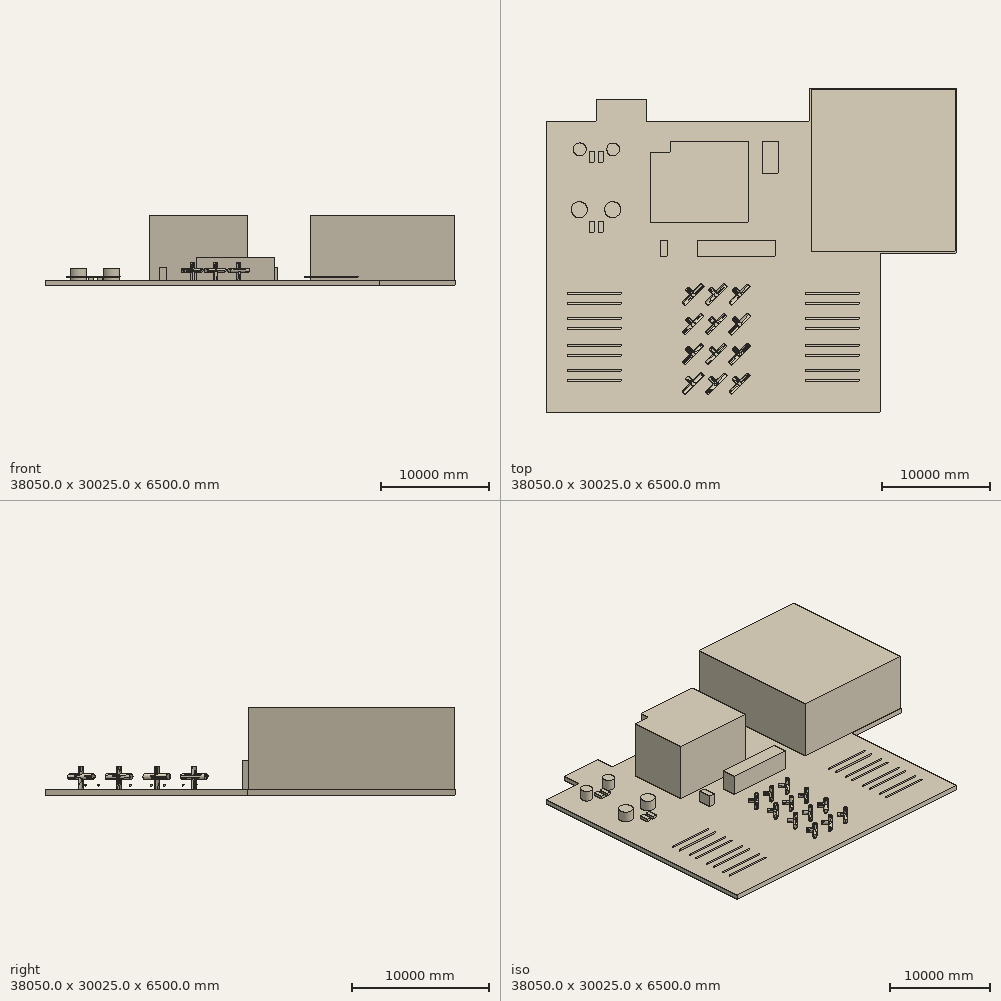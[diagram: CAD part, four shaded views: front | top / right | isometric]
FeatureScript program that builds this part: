
annotation { "Feature Type Name" : "Feature", "Feature Type Description" : "" }
export const myFeature = defineFeature(function(context is Context, id is Id, definition is map)
    precondition{}
    {
        {
            var Q0;
            Q0=qCreatedBy(makeId("Top.planeOp"),FACE);
            var sketch = newSketch(context, id + "F0", { "sketchPlane" : qUnion([Q0])});
            skLineSegment(sketch, "E0", {"start": v(0, 0) * mm, "end": v(31000, 0) * mm});
            skLineSegment(sketch, "E1", {"start": v(31000, 0) * mm, "end": v(31000, 14775) * mm});
            skLineSegment(sketch, "E2", {"start": v(31000, 14775) * mm, "end": v(38050, 14775) * mm});
            skLineSegment(sketch, "E3", {"start": v(38050, 14775) * mm, "end": v(38050, 30025) * mm});
            skLineSegment(sketch, "E4", {"start": v(38050, 30025) * mm, "end": v(24450, 30025) * mm});
            skLineSegment(sketch, "E5", {"start": v(24450, 30025) * mm, "end": v(24450, 26990) * mm});
            skLineSegment(sketch, "E6", {"start": v(24450, 26990) * mm, "end": v(0, 26990) * mm});
            skLineSegment(sketch, "E7", {"start": v(0, 26990) * mm, "end": v(0, 0) * mm});
            skLineSegment(sketch, "E8", {"start": v(4600, 26990) * mm, "end": v(4600, 28990) * mm});
            skLineSegment(sketch, "E9", {"start": v(4600, 28990) * mm, "end": v(9300, 28990) * mm});
            skLineSegment(sketch, "E10", {"start": v(9300, 28990) * mm, "end": v(9300, 26990) * mm});
            skSolve(sketch);
        }
        {
            var Q0;
            Q0=makeQuery(id+"F0.imprint","IMPRINT",FACE,{"disambiguationData":[TD([[makeQuery(id+"F0.imprint","IMPRINT",EDGE,{"derivedFrom":sQuery(id+"F0.wireOp",EDGE,"E0")}),1.0]])]});
            var Q1;
            {var subQ0=sQuery(id+"F0.wireOp",EDGE,"E8");Q1=makeQuery(id+"F0.imprint","IMPRINT",FACE,{"disambiguationData":[TD([[makeQuery(id+"F0.imprint","IMPRINT",EDGE,{"derivedFrom":subQ0}),-1.0]])]});}
            extrude(context, id + "F1", {"entities" : qUnion([Q0, Q1]), "depth" : 500 * mm, "offsetDistance" : 25 * mm});
        }
        {
            var Q0;
            Q0=makeQuery(id+"F1.opExtrude","CAP_FACE",FACE,{"disambiguationData":[OSD([sQuery(id+"F0.wireOp",EDGE,"E0"),sQuery(id+"F0.wireOp",EDGE,"E1"),sQuery(id+"F0.wireOp",EDGE,"E2"),sQuery(id+"F0.wireOp",EDGE,"E3"),sQuery(id+"F0.wireOp",EDGE,"E4"),sQuery(id+"F0.wireOp",EDGE,"E5"),sQuery(id+"F0.wireOp",EDGE,"E6"),sQuery(id+"F0.wireOp",EDGE,"E7"),sQuery(id+"F0.wireOp",EDGE,"E8"),sQuery(id+"F0.wireOp",EDGE,"E9"),sQuery(id+"F0.wireOp",EDGE,"E10")])],"isStart":false});
            var sketch = newSketch(context, id + "F2", { "sketchPlane" : qUnion([Q0])});
            skLineSegment(sketch, "E11.0", {"start": v(37950, 14875) * mm, "end": v(37950, 29925) * mm});
            skLineSegment(sketch, "E12.0", {"start": v(37950, 29925) * mm, "end": v(24550, 29925) * mm});
            skLineSegment(sketch, "E13.0", {"start": v(24550, 14875) * mm, "end": v(37950, 14875) * mm});
            skLineSegment(sketch, "E14.0", {"start": v(24550, 29925) * mm, "end": v(24550, 14875) * mm});
            skSolve(sketch);
        }
        {
            var Q0;
            Q0=makeQuery(id+"F2.imprint","IMPRINT",FACE,{"disambiguationData":[TD([[makeQuery(id+"F2.imprint","IMPRINT",EDGE,{"derivedFrom":sQuery(id+"F2.wireOp",EDGE,"E11.0")}),1.0]])]});
            extrude(context, id + "F3", {"entities" : qUnion([Q0]), "depth" : 6000 * mm, "offsetDistance" : 25 * mm});
        }
        {
            var Q0;
            Q0=makeQuery(id+"F1.opExtrude","CAP_FACE",FACE,{"disambiguationData":[OSD([sQuery(id+"F0.wireOp",EDGE,"E0"),sQuery(id+"F0.wireOp",EDGE,"E1"),sQuery(id+"F0.wireOp",EDGE,"E2"),sQuery(id+"F0.wireOp",EDGE,"E3"),sQuery(id+"F0.wireOp",EDGE,"E4"),sQuery(id+"F0.wireOp",EDGE,"E5"),sQuery(id+"F0.wireOp",EDGE,"E6"),sQuery(id+"F0.wireOp",EDGE,"E7"),sQuery(id+"F0.wireOp",EDGE,"E8"),sQuery(id+"F0.wireOp",EDGE,"E9"),sQuery(id+"F0.wireOp",EDGE,"E10")])],"isStart":false});
            var sketch = newSketch(context, id + "F4", { "sketchPlane" : qUnion([Q0])});
            skLineSegment(sketch, "E15", {"start": v(9670, 24090) * mm, "end": v(9670, 17655) * mm});
            skLineSegment(sketch, "E16", {"start": v(9670, 17655) * mm, "end": v(18770, 17655) * mm});
            skLineSegment(sketch, "E17", {"start": v(18770, 17655) * mm, "end": v(18770, 25140) * mm});
            skLineSegment(sketch, "E18", {"start": v(18770, 25140) * mm, "end": v(11520, 25140) * mm});
            skLineSegment(sketch, "E19", {"start": v(11520, 25140) * mm, "end": v(11520, 24090) * mm});
            skLineSegment(sketch, "E20", {"start": v(11520, 24090) * mm, "end": v(9670, 24090) * mm});
            skSolve(sketch);
        }
        {
            var Q0;
            Q0=makeQuery(id+"F4.imprint","IMPRINT",FACE,{"disambiguationData":[TD([[makeQuery(id+"F4.imprint","IMPRINT",EDGE,{"derivedFrom":sQuery(id+"F4.wireOp",EDGE,"E15")}),1.0]])]});
            extrude(context, id + "F5", {"entities" : qUnion([Q0]), "depth" : 6000 * mm, "offsetDistance" : 25 * mm});
        }
        {
            var Q0;
            Q0=makeQuery(id+"F1.opExtrude","CAP_FACE",FACE,{"disambiguationData":[OSD([sQuery(id+"F0.wireOp",EDGE,"E0"),sQuery(id+"F0.wireOp",EDGE,"E1"),sQuery(id+"F0.wireOp",EDGE,"E2"),sQuery(id+"F0.wireOp",EDGE,"E3"),sQuery(id+"F0.wireOp",EDGE,"E4"),sQuery(id+"F0.wireOp",EDGE,"E5"),sQuery(id+"F0.wireOp",EDGE,"E6"),sQuery(id+"F0.wireOp",EDGE,"E7"),sQuery(id+"F0.wireOp",EDGE,"E8"),sQuery(id+"F0.wireOp",EDGE,"E9"),sQuery(id+"F0.wireOp",EDGE,"E10")])],"isStart":false});
            var sketch = newSketch(context, id + "F6", { "sketchPlane" : qUnion([Q0])});
            skLineSegment(sketch, "E21.bottom", {"start": v(14054, 15955) * mm, "end": v(21254, 15955) * mm});
            skLineSegment(sketch, "E21.top", {"start": v(14054, 14455) * mm, "end": v(21254, 14455) * mm});
            skLineSegment(sketch, "E21.left", {"start": v(14054, 15955) * mm, "end": v(14054, 14455) * mm});
            skLineSegment(sketch, "E21.right", {"start": v(21254, 15955) * mm, "end": v(21254, 14455) * mm});
            skSolve(sketch);
        }
        {
            var Q0;
            Q0=makeQuery(id+"F6.imprint","IMPRINT",FACE,{"disambiguationData":[TD([[makeQuery(id+"F6.imprint","IMPRINT",EDGE,{"derivedFrom":sQuery(id+"F6.wireOp",EDGE,"E21.bottom")}),-1.0]])]});
            extrude(context, id + "F7", {"entities" : qUnion([Q0]), "depth" : 2100 * mm, "offsetDistance" : 25 * mm});
        }
        {
            var Q0;
            Q0=makeQuery(id+"F1.opExtrude","CAP_FACE",FACE,{"disambiguationData":[OSD([sQuery(id+"F0.wireOp",EDGE,"E0"),sQuery(id+"F0.wireOp",EDGE,"E1"),sQuery(id+"F0.wireOp",EDGE,"E2"),sQuery(id+"F0.wireOp",EDGE,"E3"),sQuery(id+"F0.wireOp",EDGE,"E4"),sQuery(id+"F0.wireOp",EDGE,"E5"),sQuery(id+"F0.wireOp",EDGE,"E6"),sQuery(id+"F0.wireOp",EDGE,"E7"),sQuery(id+"F0.wireOp",EDGE,"E8"),sQuery(id+"F0.wireOp",EDGE,"E9"),sQuery(id+"F0.wireOp",EDGE,"E10")])],"isStart":false});
            var sketch = newSketch(context, id + "F8", { "sketchPlane" : qUnion([Q0])});
            skLineSegment(sketch, "E22.bottom", {"start": v(2000, 25190) * mm, "end": v(7300, 25190) * mm});
            skLineSegment(sketch, "E22.top", {"start": v(2000, 22390) * mm, "end": v(7300, 22390) * mm});
            skLineSegment(sketch, "E22.left", {"start": v(2000, 25190) * mm, "end": v(2000, 22390) * mm});
            skLineSegment(sketch, "E22.right", {"start": v(7300, 25190) * mm, "end": v(7300, 22390) * mm});
            skLineSegment(sketch, "E23.bottom", {"start": v(1955.55, 19990) * mm, "end": v(7255.55, 19990) * mm});
            skLineSegment(sketch, "E23.top", {"start": v(1955.55, 16190) * mm, "end": v(7255.55, 16190) * mm});
            skLineSegment(sketch, "E23.left", {"start": v(1955.55, 19990) * mm, "end": v(1955.55, 16190) * mm});
            skLineSegment(sketch, "E23.right", {"start": v(7255.55, 19990) * mm, "end": v(7255.55, 16190) * mm});
            skCircle(sketch, "E24", {"center": v(3100, 24390) * mm, "radius": 600 * mm});
            skCircle(sketch, "E25", {"center": v(6200, 24390) * mm, "radius": 600 * mm});
            skCircle(sketch, "E26", {"center": v(3055.55, 18790) * mm, "radius": 750 * mm});
            skCircle(sketch, "E27", {"center": v(6155.55, 18790) * mm, "radius": 750 * mm});
            skSolve(sketch);
        }
        {
            var Q0;
            Q0=makeQuery(id+"F8.imprint","IMPRINT",FACE,{"disambiguationData":[TD([[makeQuery(id+"F8.imprint","IMPRINT",EDGE,{"derivedFrom":sQuery(id+"F8.wireOp",EDGE,"E24")}),1.0]])]});
            var Q1;
            Q1=makeQuery(id+"F8.imprint","IMPRINT",FACE,{"disambiguationData":[TD([[makeQuery(id+"F8.imprint","IMPRINT",EDGE,{"derivedFrom":sQuery(id+"F8.wireOp",EDGE,"E25")}),1.0]])]});
            var Q2;
            Q2=makeQuery(id+"F8.imprint","IMPRINT",FACE,{"disambiguationData":[TD([[makeQuery(id+"F8.imprint","IMPRINT",EDGE,{"derivedFrom":sQuery(id+"F8.wireOp",EDGE,"E26")}),1.0]])]});
            var Q3;
            Q3=makeQuery(id+"F8.imprint","IMPRINT",FACE,{"disambiguationData":[TD([[makeQuery(id+"F8.imprint","IMPRINT",EDGE,{"derivedFrom":sQuery(id+"F8.wireOp",EDGE,"E27")}),1.0]])]});
            extrude(context, id + "F9", {"entities" : qUnion([Q0, Q1, Q2, Q3]), "depth" : 1100 * mm, "offsetDistance" : 25 * mm});
        }
        {
            var Q0;
            Q0=makeQuery(id+"F1.opExtrude","CAP_FACE",FACE,{"disambiguationData":[OSD([sQuery(id+"F0.wireOp",EDGE,"E0"),sQuery(id+"F0.wireOp",EDGE,"E1"),sQuery(id+"F0.wireOp",EDGE,"E2"),sQuery(id+"F0.wireOp",EDGE,"E3"),sQuery(id+"F0.wireOp",EDGE,"E4"),sQuery(id+"F0.wireOp",EDGE,"E5"),sQuery(id+"F0.wireOp",EDGE,"E6"),sQuery(id+"F0.wireOp",EDGE,"E7"),sQuery(id+"F0.wireOp",EDGE,"E8"),sQuery(id+"F0.wireOp",EDGE,"E9"),sQuery(id+"F0.wireOp",EDGE,"E10")])],"isStart":false});
            var sketch = newSketch(context, id + "F10", { "sketchPlane" : qUnion([Q0])});
            skLineSegment(sketch, "E28.bottom", {"start": v(4000, 24190) * mm, "end": v(4500, 24190) * mm});
            skLineSegment(sketch, "E28.top", {"start": v(4000, 23190) * mm, "end": v(4500, 23190) * mm});
            skLineSegment(sketch, "E28.left", {"start": v(4000, 24190) * mm, "end": v(4000, 23190) * mm});
            skLineSegment(sketch, "E28.right", {"start": v(4500, 24190) * mm, "end": v(4500, 23190) * mm});
            skLineSegment(sketch, "E29.bottom", {"start": v(4800, 24190) * mm, "end": v(5300, 24190) * mm});
            skLineSegment(sketch, "E29.top", {"start": v(4800, 23190) * mm, "end": v(5300, 23190) * mm});
            skLineSegment(sketch, "E29.left", {"start": v(4800, 24190) * mm, "end": v(4800, 23190) * mm});
            skLineSegment(sketch, "E29.right", {"start": v(5300, 24190) * mm, "end": v(5300, 23190) * mm});
            skLineSegment(sketch, "E30.bottom", {"start": v(3980.54, 17694.12) * mm, "end": v(4480.54, 17694.12) * mm});
            skLineSegment(sketch, "E30.top", {"start": v(3980.54, 16694.12) * mm, "end": v(4480.54, 16694.12) * mm});
            skLineSegment(sketch, "E30.left", {"start": v(3980.54, 17694.12) * mm, "end": v(3980.54, 16694.12) * mm});
            skLineSegment(sketch, "E30.right", {"start": v(4480.54, 17694.12) * mm, "end": v(4480.54, 16694.12) * mm});
            skLineSegment(sketch, "E31.bottom", {"start": v(4780.54, 17694.12) * mm, "end": v(5280.54, 17694.12) * mm});
            skLineSegment(sketch, "E31.top", {"start": v(4780.54, 16694.12) * mm, "end": v(5280.54, 16694.12) * mm});
            skLineSegment(sketch, "E31.left", {"start": v(4780.54, 17694.12) * mm, "end": v(4780.54, 16694.12) * mm});
            skLineSegment(sketch, "E31.right", {"start": v(5280.54, 17694.12) * mm, "end": v(5280.54, 16694.12) * mm});
            skSolve(sketch);
        }
        {
            var Q0;
            Q0=makeQuery(id+"F10.imprint","IMPRINT",FACE,{"disambiguationData":[TD([[makeQuery(id+"F10.imprint","IMPRINT",EDGE,{"derivedFrom":sQuery(id+"F10.wireOp",EDGE,"E28.bottom")}),-1.0]])]});
            var Q1;
            Q1=makeQuery(id+"F10.imprint","IMPRINT",FACE,{"disambiguationData":[TD([[makeQuery(id+"F10.imprint","IMPRINT",EDGE,{"derivedFrom":sQuery(id+"F10.wireOp",EDGE,"E29.bottom")}),-1.0]])]});
            var Q2;
            Q2=makeQuery(id+"F10.imprint","IMPRINT",FACE,{"disambiguationData":[TD([[makeQuery(id+"F10.imprint","IMPRINT",EDGE,{"derivedFrom":sQuery(id+"F10.wireOp",EDGE,"E30.bottom")}),-1.0]])]});
            var Q3;
            Q3=makeQuery(id+"F10.imprint","IMPRINT",FACE,{"disambiguationData":[TD([[makeQuery(id+"F10.imprint","IMPRINT",EDGE,{"derivedFrom":sQuery(id+"F10.wireOp",EDGE,"E31.bottom")}),-1.0]])]});
            extrude(context, id + "F11", {"entities" : qUnion([Q0, Q1, Q2, Q3]), "depth" : 300 * mm, "offsetDistance" : 25 * mm});
        }
        {
            var Q0;
            Q0=makeQuery(id+"F1.opExtrude","CAP_FACE",FACE,{"disambiguationData":[OSD([sQuery(id+"F0.wireOp",EDGE,"E0"),sQuery(id+"F0.wireOp",EDGE,"E1"),sQuery(id+"F0.wireOp",EDGE,"E2"),sQuery(id+"F0.wireOp",EDGE,"E3"),sQuery(id+"F0.wireOp",EDGE,"E4"),sQuery(id+"F0.wireOp",EDGE,"E5"),sQuery(id+"F0.wireOp",EDGE,"E6"),sQuery(id+"F0.wireOp",EDGE,"E7"),sQuery(id+"F0.wireOp",EDGE,"E8"),sQuery(id+"F0.wireOp",EDGE,"E9"),sQuery(id+"F0.wireOp",EDGE,"E10")])],"isStart":false});
            var sketch = newSketch(context, id + "F12", { "sketchPlane" : qUnion([Q0])});
            skLineSegment(sketch, "E32", {"start": v(0, 0) * mm, "end": v(13620, 0) * mm, "construction": true});
            skLineSegment(sketch, "E33", {"start": v(13620, 0) * mm, "end": v(13620, 2628) * mm, "construction": true});
            skCircle(sketch, "E34", {"center": v(13620, 2628) * mm, "radius": 190.5 * mm});
            skSolve(sketch);
        }
        {
            var Q0;
            Q0=makeQuery(id+"F12.imprint","IMPRINT",FACE,{"disambiguationData":[TD([[makeQuery(id+"F12.imprint","IMPRINT",EDGE,{"derivedFrom":sQuery(id+"F12.wireOp",EDGE,"E34")}),1.0]])]});
            extrude(context, id + "F13", {"entities" : qUnion([Q0]), "depth" : 1615 * mm, "offsetDistance" : 25 * mm});
        }
        {
            var Q0;
            Q0=makeQuery(id+"F1.opExtrude","CAP_FACE",FACE,{"disambiguationData":[OSD([sQuery(id+"F0.wireOp",EDGE,"E0"),sQuery(id+"F0.wireOp",EDGE,"E1"),sQuery(id+"F0.wireOp",EDGE,"E2"),sQuery(id+"F0.wireOp",EDGE,"E3"),sQuery(id+"F0.wireOp",EDGE,"E4"),sQuery(id+"F0.wireOp",EDGE,"E5"),sQuery(id+"F0.wireOp",EDGE,"E6"),sQuery(id+"F0.wireOp",EDGE,"E7"),sQuery(id+"F0.wireOp",EDGE,"E8"),sQuery(id+"F0.wireOp",EDGE,"E9"),sQuery(id+"F0.wireOp",EDGE,"E10")])],"isStart":false});
            var sketch = newSketch(context, id + "F14", { "sketchPlane" : qUnion([Q0])});
            skCircle(sketch, "E35", {"center": v(15123.7, 3486.6) * mm, "radius": 209.5 * mm});
            skSolve(sketch);
        }
        {
            var Q0;
            Q0=makeQuery(id+"F14.imprint","IMPRINT",FACE,{"disambiguationData":[TD([[makeQuery(id+"F14.imprint","IMPRINT",EDGE,{"derivedFrom":sQuery(id+"F14.wireOp",EDGE,"E35")}),1.0]])]});
            extrude(context, id + "F15", {"entities" : qUnion([Q0]), "depth" : 2458 * mm, "offsetDistance" : 25 * mm});
        }
        {
            var Q0;
            Q0=makeQuery(id+"F15.opExtrude","SWEPT_BODY",BODY,{"disambiguationData":[OSD([sQuery(id+"F14.wireOp",EDGE,"E35")])]});
            var Q1;
            Q1=makeQuery(id+"F1.opExtrude","CAP_EDGE",EDGE,{"disambiguationData":[OSD([sQuery(id+"F0.wireOp",EDGE,"E0")])],"isStart":false});
            transform(context, id + "F16", {"entities" : qUnion([Q0]), "transformType" : TransformType.ROTATION, "transformAxis" : qUnion([Q1]), "angle" : 90 * degree, "makeCopy" : false});
        }
        {
            var Q0;
            Q0=makeQuery(id+"F15.opExtrude","SWEPT_BODY",BODY,{"disambiguationData":[OSD([sQuery(id+"F14.wireOp",EDGE,"E35")])]});
            transform(context, id + "F17", {"entities" : qUnion([Q0]), "transformType" : TransformType.TRANSLATION_3D, "dx" : -1510 * mm, "dy" : 3860 * mm, "dz" : -2600 * mm, "makeCopy" : false});
        }
        {
            var Q0;
            Q0=makeQuery(id+"F15.opExtrude","SWEPT_BODY",BODY,{"disambiguationData":[OSD([sQuery(id+"F14.wireOp",EDGE,"E35")])]});
            transform(context, id + "F18", {"entities" : qUnion([Q0]), "transformType" : TransformType.TRANSLATION_3D, "dx" : 0 * mm, "dy" : 0 * mm, "dz" : 939 * mm, "makeCopy" : false});
        }
        {
            var Q0;
            Q0=makeQuery(id+"F15.opExtrude","SWEPT_BODY",BODY,{"disambiguationData":[OSD([sQuery(id+"F14.wireOp",EDGE,"E35")])]});
            transform(context, id + "F19", {"entities" : qUnion([Q0]), "transformType" : TransformType.TRANSLATION_3D, "dx" : 0 * mm, "dy" : 0 * mm, "dz" : -930 * mm, "makeCopy" : false});
        }
        {
            var Q0;
            Q0=makeQuery(id+"F15.opExtrude","SWEPT_BODY",BODY,{"disambiguationData":[OSD([sQuery(id+"F14.wireOp",EDGE,"E35")])]});
            var Q1;
            Q1=makeQuery(id+"F13.opExtrude","SWEPT_FACE",FACE,{"disambiguationData":[OSD([sQuery(id+"F12.wireOp",EDGE,"E34")])]});
            transform(context, id + "F20", {"entities" : qUnion([Q0]), "transformType" : TransformType.ROTATION, "transformAxis" : qUnion([Q1]), "angle" : 45 * degree, "makeCopy" : false});
        }
        {
            var Q0;
            Q0=makeQuery(id+"F1.opExtrude","CAP_FACE",FACE,{"disambiguationData":[OSD([sQuery(id+"F0.wireOp",EDGE,"E0"),sQuery(id+"F0.wireOp",EDGE,"E1"),sQuery(id+"F0.wireOp",EDGE,"E2"),sQuery(id+"F0.wireOp",EDGE,"E3"),sQuery(id+"F0.wireOp",EDGE,"E4"),sQuery(id+"F0.wireOp",EDGE,"E5"),sQuery(id+"F0.wireOp",EDGE,"E6"),sQuery(id+"F0.wireOp",EDGE,"E7"),sQuery(id+"F0.wireOp",EDGE,"E8"),sQuery(id+"F0.wireOp",EDGE,"E9"),sQuery(id+"F0.wireOp",EDGE,"E10")])],"isStart":false});
            var sketch = newSketch(context, id + "F21", { "sketchPlane" : qUnion([Q0])});
            skCircle(sketch, "E36", {"center": v(10922.38, 1929.03) * mm, "radius": 207 * mm});
            skSolve(sketch);
        }
        {
            var Q0;
            Q0=makeQuery(id+"F21.imprint","IMPRINT",FACE,{"disambiguationData":[TD([[makeQuery(id+"F21.imprint","IMPRINT",EDGE,{"derivedFrom":sQuery(id+"F21.wireOp",EDGE,"E36")}),1.0]])]});
            extrude(context, id + "F22", {"entities" : qUnion([Q0]), "depth" : 955 * mm, "offsetDistance" : 25 * mm});
        }
        {
            var Q0;
            Q0=makeQuery(id+"F22.opExtrude","SWEPT_BODY",BODY,{"disambiguationData":[OSD([sQuery(id+"F21.wireOp",EDGE,"E36")])]});
            var Q1;
            Q1=makeQuery(id+"F1.opExtrude","CAP_EDGE",EDGE,{"disambiguationData":[OSD([sQuery(id+"F0.wireOp",EDGE,"E0")])],"isStart":false});
            transform(context, id + "F23", {"entities" : qUnion([Q0]), "transformType" : TransformType.ROTATION, "transformAxis" : qUnion([Q1]), "angle" : 90 * degree, "makeCopy" : false});
        }
        {
            var Q0;
            Q0=makeQuery(id+"F22.opExtrude","SWEPT_BODY",BODY,{"disambiguationData":[OSD([sQuery(id+"F21.wireOp",EDGE,"E36")])]});
            transform(context, id + "F24", {"entities" : qUnion([Q0]), "transformType" : TransformType.TRANSLATION_3D, "dx" : 2700 * mm, "dy" : 3450 * mm, "dz" : -1023 * mm, "makeCopy" : false});
        }
        {
            var Q0;
            Q0=makeQuery(id+"F22.opExtrude","SWEPT_BODY",BODY,{"disambiguationData":[OSD([sQuery(id+"F21.wireOp",EDGE,"E36")])]});
            var Q1;
            Q1=makeQuery(id+"F13.opExtrude","SWEPT_FACE",FACE,{"disambiguationData":[OSD([sQuery(id+"F12.wireOp",EDGE,"E34")])]});
            transform(context, id + "F25", {"entities" : qUnion([Q0]), "transformType" : TransformType.ROTATION, "transformAxis" : qUnion([Q1]), "angle" : 315 * degree, "makeCopy" : false});
        }
        {
            var Q0;
            Q0=makeQuery(id+"F15.opExtrude","SWEPT_BODY",BODY,{"disambiguationData":[OSD([sQuery(id+"F14.wireOp",EDGE,"E35")])]});
            var Q1;
            Q1=makeQuery(id+"F22.opExtrude","SWEPT_BODY",BODY,{"disambiguationData":[OSD([sQuery(id+"F21.wireOp",EDGE,"E36")])]});
            var Q2;
            Q2=makeQuery(id+"F13.opExtrude","SWEPT_BODY",BODY,{"disambiguationData":[OSD([sQuery(id+"F12.wireOp",EDGE,"E34")])]});
            booleanBodies(context, id + "F26", {"operationType" : BooleanOperationType.UNION, "tools" : qUnion([Q0, Q1, Q2])});
        }
        {
            var Q0;
            Q0=makeQuery(id+"F1.opExtrude","CAP_FACE",FACE,{"disambiguationData":[OSD([sQuery(id+"F0.wireOp",EDGE,"E0"),sQuery(id+"F0.wireOp",EDGE,"E1"),sQuery(id+"F0.wireOp",EDGE,"E2"),sQuery(id+"F0.wireOp",EDGE,"E3"),sQuery(id+"F0.wireOp",EDGE,"E4"),sQuery(id+"F0.wireOp",EDGE,"E5"),sQuery(id+"F0.wireOp",EDGE,"E6"),sQuery(id+"F0.wireOp",EDGE,"E7"),sQuery(id+"F0.wireOp",EDGE,"E8"),sQuery(id+"F0.wireOp",EDGE,"E9"),sQuery(id+"F0.wireOp",EDGE,"E10")])],"isStart":false});
            var sketch = newSketch(context, id + "F27", { "sketchPlane" : qUnion([Q0])});
            skLineSegment(sketch, "E37", {"start": v(0, 0) * mm, "end": v(15500, 0) * mm, "construction": true});
            skLineSegment(sketch, "E38", {"start": v(15500, 0) * mm, "end": v(15500, 2628) * mm, "construction": true});
            skLineSegment(sketch, "E39", {"start": v(15500, 2628) * mm, "end": v(17938, 2628) * mm, "construction": true});
            skSolve(sketch);
        }
        {
            var Q0;
            Q0=makeQuery(id+"F15.opExtrude","SWEPT_BODY",BODY,{"disambiguationData":[OSD([sQuery(id+"F14.wireOp",EDGE,"E35")])]});
            transform(context, id + "F28", {"entities" : qUnion([Q0]), "transformType" : TransformType.COPY});
        }
        {
            var Q0;
            Q0=makeQuery(id+"F15.opExtrude","SWEPT_BODY",BODY,{"disambiguationData":[OSD([sQuery(id+"F14.wireOp",EDGE,"E35")])]});
            var Q1;
            Q1=makeQuery(id+"F28.opPattern","COPY",BODY,{"derivedFrom":makeQuery(id+"F15.opExtrude","SWEPT_BODY",BODY,{"disambiguationData":[OSD([sQuery(id+"F14.wireOp",EDGE,"E35")])]}),"instanceName":"1"});
            transform(context, id + "F29", {"entities" : qUnion([Q0, Q1]), "transformType" : TransformType.TRANSLATION_3D, "dx" : 1882 * mm, "dy" : 0 * mm, "dz" : 0 * mm, "makeCopy" : true});
        }
        {
            var Q0;
            Q0=makeQuery(id+"F29.opPattern","COPY",BODY,{"derivedFrom":makeQuery(id+"F15.opExtrude","SWEPT_BODY",BODY,{"disambiguationData":[OSD([sQuery(id+"F14.wireOp",EDGE,"E35")])]}),"instanceName":"1"});
            var Q1;
            Q1=makeQuery(id+"F29.opPattern","COPY",BODY,{"derivedFrom":makeQuery(id+"F28.opPattern","COPY",BODY,{"derivedFrom":makeQuery(id+"F15.opExtrude","SWEPT_BODY",BODY,{"disambiguationData":[OSD([sQuery(id+"F14.wireOp",EDGE,"E35")])]}),"instanceName":"1"}),"instanceName":"1"});
            transform(context, id + "F30", {"entities" : qUnion([Q0, Q1]), "transformType" : TransformType.TRANSLATION_3D, "dx" : 2436 * mm, "dy" : 0 * mm, "dz" : 0 * mm, "makeCopy" : true});
        }
        {
            var Q0;
            Q0=makeQuery(id+"F29.opPattern","COPY",BODY,{"derivedFrom":makeQuery(id+"F15.opExtrude","SWEPT_BODY",BODY,{"disambiguationData":[OSD([sQuery(id+"F14.wireOp",EDGE,"E35")])]}),"instanceName":"1"});
            var Q1;
            Q1=makeQuery(id+"F29.opPattern","COPY",BODY,{"derivedFrom":makeQuery(id+"F28.opPattern","COPY",BODY,{"derivedFrom":makeQuery(id+"F15.opExtrude","SWEPT_BODY",BODY,{"disambiguationData":[OSD([sQuery(id+"F14.wireOp",EDGE,"E35")])]}),"instanceName":"1"}),"instanceName":"1"});
            transform(context, id + "F31", {"entities" : qUnion([Q0, Q1]), "transformType" : TransformType.TRANSLATION_3D, "dx" : 260 * mm, "dy" : 0 * mm, "dz" : 0 * mm, "makeCopy" : false});
        }
        {
            var Q0;
            Q0=makeQuery(id+"F27.imprint","IMPRINT",FACE,{"disambiguationData":[TD([[makeQuery(id+"F27.imprint","IMPRINT",EDGE,{"derivedFrom":makeQuery(id+"F1.opExtrude","CAP_EDGE",EDGE,{"disambiguationData":[OSD([sQuery(id+"F0.wireOp",EDGE,"E0")])],"isStart":false})}),1.0]])]});
            var sketch = newSketch(context, id + "F32", { "sketchPlane" : qUnion([Q0])});
            skLineSegment(sketch, "E40", {"start": v(15494.88, 2638.74) * mm, "end": v(15494.88, 5381.74) * mm, "construction": true});
            skLineSegment(sketch, "E41", {"start": v(15494.88, 5381.74) * mm, "end": v(15494.88, 8124.74) * mm, "construction": true});
            skLineSegment(sketch, "E42", {"start": v(15494.88, 8124.74) * mm, "end": v(15494.88, 10867.74) * mm, "construction": true});
            skSolve(sketch);
        }
        {
            var Q0;
            Q0=makeQuery(id+"F15.opExtrude","SWEPT_BODY",BODY,{"disambiguationData":[OSD([sQuery(id+"F14.wireOp",EDGE,"E35")])]});
            var Q1;
            Q1=makeQuery(id+"F29.opPattern","COPY",BODY,{"derivedFrom":makeQuery(id+"F15.opExtrude","SWEPT_BODY",BODY,{"disambiguationData":[OSD([sQuery(id+"F14.wireOp",EDGE,"E35")])]}),"instanceName":"1"});
            var Q2;
            Q2=makeQuery(id+"F30.opPattern","COPY",BODY,{"derivedFrom":makeQuery(id+"F29.opPattern","COPY",BODY,{"derivedFrom":makeQuery(id+"F15.opExtrude","SWEPT_BODY",BODY,{"disambiguationData":[OSD([sQuery(id+"F14.wireOp",EDGE,"E35")])]}),"instanceName":"1"}),"instanceName":"1"});
            var Q3;
            Q3=makeQuery(id+"F29.opPattern","COPY",BODY,{"derivedFrom":makeQuery(id+"F28.opPattern","COPY",BODY,{"derivedFrom":makeQuery(id+"F15.opExtrude","SWEPT_BODY",BODY,{"disambiguationData":[OSD([sQuery(id+"F14.wireOp",EDGE,"E35")])]}),"instanceName":"1"}),"instanceName":"1"});
            var Q4;
            Q4=makeQuery(id+"F30.opPattern","COPY",BODY,{"derivedFrom":makeQuery(id+"F29.opPattern","COPY",BODY,{"derivedFrom":makeQuery(id+"F28.opPattern","COPY",BODY,{"derivedFrom":makeQuery(id+"F15.opExtrude","SWEPT_BODY",BODY,{"disambiguationData":[OSD([sQuery(id+"F14.wireOp",EDGE,"E35")])]}),"instanceName":"1"}),"instanceName":"1"}),"instanceName":"1"});
            var Q5;
            Q5=makeQuery(id+"F28.opPattern","COPY",BODY,{"derivedFrom":makeQuery(id+"F15.opExtrude","SWEPT_BODY",BODY,{"disambiguationData":[OSD([sQuery(id+"F14.wireOp",EDGE,"E35")])]}),"instanceName":"1"});
            transform(context, id + "F33", {"entities" : qUnion([Q0, Q1, Q2, Q3, Q4, Q5]), "transformType" : TransformType.TRANSLATION_3D, "dx" : 0 * mm, "dy" : 2760 * mm, "dz" : 0 * mm, "makeCopy" : true});
        }
        {
            var Q0;
            Q0=makeQuery(id+"F33.opPattern","COPY",BODY,{"derivedFrom":makeQuery(id+"F15.opExtrude","SWEPT_BODY",BODY,{"disambiguationData":[OSD([sQuery(id+"F14.wireOp",EDGE,"E35")])]}),"instanceName":"1"});
            var Q1;
            Q1=makeQuery(id+"F33.opPattern","COPY",BODY,{"derivedFrom":makeQuery(id+"F29.opPattern","COPY",BODY,{"derivedFrom":makeQuery(id+"F15.opExtrude","SWEPT_BODY",BODY,{"disambiguationData":[OSD([sQuery(id+"F14.wireOp",EDGE,"E35")])]}),"instanceName":"1"}),"instanceName":"1"});
            var Q2;
            Q2=makeQuery(id+"F33.opPattern","COPY",BODY,{"derivedFrom":makeQuery(id+"F30.opPattern","COPY",BODY,{"derivedFrom":makeQuery(id+"F29.opPattern","COPY",BODY,{"derivedFrom":makeQuery(id+"F15.opExtrude","SWEPT_BODY",BODY,{"disambiguationData":[OSD([sQuery(id+"F14.wireOp",EDGE,"E35")])]}),"instanceName":"1"}),"instanceName":"1"}),"instanceName":"1"});
            var Q3;
            Q3=makeQuery(id+"F33.opPattern","COPY",BODY,{"derivedFrom":makeQuery(id+"F29.opPattern","COPY",BODY,{"derivedFrom":makeQuery(id+"F28.opPattern","COPY",BODY,{"derivedFrom":makeQuery(id+"F15.opExtrude","SWEPT_BODY",BODY,{"disambiguationData":[OSD([sQuery(id+"F14.wireOp",EDGE,"E35")])]}),"instanceName":"1"}),"instanceName":"1"}),"instanceName":"1"});
            var Q4;
            Q4=makeQuery(id+"F33.opPattern","COPY",BODY,{"derivedFrom":makeQuery(id+"F28.opPattern","COPY",BODY,{"derivedFrom":makeQuery(id+"F15.opExtrude","SWEPT_BODY",BODY,{"disambiguationData":[OSD([sQuery(id+"F14.wireOp",EDGE,"E35")])]}),"instanceName":"1"}),"instanceName":"1"});
            var Q5;
            Q5=makeQuery(id+"F33.opPattern","COPY",BODY,{"derivedFrom":makeQuery(id+"F30.opPattern","COPY",BODY,{"derivedFrom":makeQuery(id+"F29.opPattern","COPY",BODY,{"derivedFrom":makeQuery(id+"F28.opPattern","COPY",BODY,{"derivedFrom":makeQuery(id+"F15.opExtrude","SWEPT_BODY",BODY,{"disambiguationData":[OSD([sQuery(id+"F14.wireOp",EDGE,"E35")])]}),"instanceName":"1"}),"instanceName":"1"}),"instanceName":"1"}),"instanceName":"1"});
            transform(context, id + "F34", {"entities" : qUnion([Q0, Q1, Q2, Q3, Q4, Q5]), "transformType" : TransformType.TRANSLATION_3D, "dx" : 0 * mm, "dy" : 2760 * mm, "dz" : 0 * mm, "makeCopy" : true});
        }
        {
            var Q0;
            Q0=makeQuery(id+"F34.opPattern","COPY",BODY,{"derivedFrom":makeQuery(id+"F33.opPattern","COPY",BODY,{"derivedFrom":makeQuery(id+"F30.opPattern","COPY",BODY,{"derivedFrom":makeQuery(id+"F29.opPattern","COPY",BODY,{"derivedFrom":makeQuery(id+"F15.opExtrude","SWEPT_BODY",BODY,{"disambiguationData":[OSD([sQuery(id+"F14.wireOp",EDGE,"E35")])]}),"instanceName":"1"}),"instanceName":"1"}),"instanceName":"1"}),"instanceName":"1"});
            var Q1;
            Q1=makeQuery(id+"F34.opPattern","COPY",BODY,{"derivedFrom":makeQuery(id+"F33.opPattern","COPY",BODY,{"derivedFrom":makeQuery(id+"F29.opPattern","COPY",BODY,{"derivedFrom":makeQuery(id+"F15.opExtrude","SWEPT_BODY",BODY,{"disambiguationData":[OSD([sQuery(id+"F14.wireOp",EDGE,"E35")])]}),"instanceName":"1"}),"instanceName":"1"}),"instanceName":"1"});
            var Q2;
            Q2=makeQuery(id+"F34.opPattern","COPY",BODY,{"derivedFrom":makeQuery(id+"F33.opPattern","COPY",BODY,{"derivedFrom":makeQuery(id+"F15.opExtrude","SWEPT_BODY",BODY,{"disambiguationData":[OSD([sQuery(id+"F14.wireOp",EDGE,"E35")])]}),"instanceName":"1"}),"instanceName":"1"});
            var Q3;
            Q3=makeQuery(id+"F34.opPattern","COPY",BODY,{"derivedFrom":makeQuery(id+"F33.opPattern","COPY",BODY,{"derivedFrom":makeQuery(id+"F30.opPattern","COPY",BODY,{"derivedFrom":makeQuery(id+"F29.opPattern","COPY",BODY,{"derivedFrom":makeQuery(id+"F28.opPattern","COPY",BODY,{"derivedFrom":makeQuery(id+"F15.opExtrude","SWEPT_BODY",BODY,{"disambiguationData":[OSD([sQuery(id+"F14.wireOp",EDGE,"E35")])]}),"instanceName":"1"}),"instanceName":"1"}),"instanceName":"1"}),"instanceName":"1"}),"instanceName":"1"});
            var Q4;
            Q4=makeQuery(id+"F34.opPattern","COPY",BODY,{"derivedFrom":makeQuery(id+"F33.opPattern","COPY",BODY,{"derivedFrom":makeQuery(id+"F29.opPattern","COPY",BODY,{"derivedFrom":makeQuery(id+"F28.opPattern","COPY",BODY,{"derivedFrom":makeQuery(id+"F15.opExtrude","SWEPT_BODY",BODY,{"disambiguationData":[OSD([sQuery(id+"F14.wireOp",EDGE,"E35")])]}),"instanceName":"1"}),"instanceName":"1"}),"instanceName":"1"}),"instanceName":"1"});
            var Q5;
            Q5=makeQuery(id+"F34.opPattern","COPY",BODY,{"derivedFrom":makeQuery(id+"F33.opPattern","COPY",BODY,{"derivedFrom":makeQuery(id+"F28.opPattern","COPY",BODY,{"derivedFrom":makeQuery(id+"F15.opExtrude","SWEPT_BODY",BODY,{"disambiguationData":[OSD([sQuery(id+"F14.wireOp",EDGE,"E35")])]}),"instanceName":"1"}),"instanceName":"1"}),"instanceName":"1"});
            transform(context, id + "F35", {"entities" : qUnion([Q0, Q1, Q2, Q3, Q4, Q5]), "transformType" : TransformType.TRANSLATION_3D, "dx" : 0 * mm, "dy" : 2740 * mm, "dz" : 0 * mm, "makeCopy" : true});
        }
        {
            var Q0;
            Q0=makeQuery(id+"F27.imprint","IMPRINT",FACE,{"disambiguationData":[TD([[makeQuery(id+"F27.imprint","IMPRINT",EDGE,{"derivedFrom":makeQuery(id+"F1.opExtrude","CAP_EDGE",EDGE,{"disambiguationData":[OSD([sQuery(id+"F0.wireOp",EDGE,"E0")])],"isStart":false})}),1.0]])]});
            var sketch = newSketch(context, id + "F36", { "sketchPlane" : qUnion([Q0])});
            skLineSegment(sketch, "E43", {"start": v(0, 0) * mm, "end": v(1500, 0) * mm, "construction": true});
            skLineSegment(sketch, "E44", {"start": v(1500, 0) * mm, "end": v(1500, 1500) * mm, "construction": true});
            skLineSegment(sketch, "E45", {"start": v(1500, 1500) * mm, "end": v(9000, 1500) * mm, "construction": true});
            skLineSegment(sketch, "E46", {"start": v(9000, 1500) * mm, "end": v(9000, 13300) * mm, "construction": true});
            skLineSegment(sketch, "E47", {"start": v(9000, 13300) * mm, "end": v(1500, 13300) * mm, "construction": true});
            skLineSegment(sketch, "E48", {"start": v(1500, 13300) * mm, "end": v(1500, 1500) * mm, "construction": true});
            skCircle(sketch, "E49", {"center": v(2614.02, 3180.53) * mm, "radius": 75 * mm});
            skSolve(sketch);
        }
        {
            var Q0;
            Q0=makeQuery(id+"F36.imprint","IMPRINT",FACE,{"disambiguationData":[TD([[makeQuery(id+"F36.imprint","IMPRINT",EDGE,{"derivedFrom":sQuery(id+"F36.wireOp",EDGE,"E49")}),1.0]])]});
            extrude(context, id + "F37", {"entities" : qUnion([Q0]), "depth" : 5000 * mm, "offsetDistance" : 25 * mm});
        }
        {
            var Q0;
            Q0=makeQuery(id+"F37.opExtrude","SWEPT_BODY",BODY,{"disambiguationData":[OSD([sQuery(id+"F36.wireOp",EDGE,"E49")])]});
            var Q1;
            Q1=sQuery(id+"F27.wireOp",EDGE,"E37");
            transform(context, id + "F38", {"entities" : qUnion([Q0]), "transformType" : TransformType.ROTATION, "transformAxis" : qUnion([Q1]), "angle" : 90 * degree, "makeCopy" : false});
        }
        {
            var Q0;
            Q0=makeQuery(id+"F37.opExtrude","SWEPT_BODY",BODY,{"disambiguationData":[OSD([sQuery(id+"F36.wireOp",EDGE,"E49")])]});
            transform(context, id + "F39", {"entities" : qUnion([Q0]), "transformType" : TransformType.TRANSLATION_3D, "dx" : 0 * mm, "dy" : 5060 * mm, "dz" : -2900 * mm, "makeCopy" : false});
        }
        {
            var Q0;
            Q0=makeQuery(id+"F37.opExtrude","SWEPT_BODY",BODY,{"disambiguationData":[OSD([sQuery(id+"F36.wireOp",EDGE,"E49")])]});
            var Q1;
            {var subQ0=sQuery(id+"F12.wireOp",EDGE,"E34");Q1=makeQuery(id+"F26.opBoolean","SPLIT",FACE,{"disambiguationData":[TD([makeQuery(id+"F13.opExtrude","CAP_FACE",FACE,{"disambiguationData":[OSD([subQ0])],"isStart":true})])],"derivedFrom":makeQuery(id+"F13.opExtrude","SWEPT_FACE",FACE,{"disambiguationData":[OSD([subQ0])]})});}
            transform(context, id + "F40", {"entities" : qUnion([Q0]), "transformType" : TransformType.ROTATION, "transformAxis" : qUnion([Q1]), "angle" : 90 * degree, "makeCopy" : false});
        }
        {
            var Q0;
            Q0=makeQuery(id+"F37.opExtrude","SWEPT_BODY",BODY,{"disambiguationData":[OSD([sQuery(id+"F36.wireOp",EDGE,"E49")])]});
            transform(context, id + "F41", {"entities" : qUnion([Q0]), "transformType" : TransformType.TRANSLATION_3D, "dx" : -9100 * mm, "dy" : -10670 * mm, "dz" : 0 * mm, "makeCopy" : false});
        }
        {
            var Q0;
            Q0=makeQuery(id+"F37.opExtrude","SWEPT_BODY",BODY,{"disambiguationData":[OSD([sQuery(id+"F36.wireOp",EDGE,"E49")])]});
            transform(context, id + "F42", {"entities" : qUnion([Q0]), "transformType" : TransformType.TRANSLATION_3D, "dx" : 0 * mm, "dy" : 940 * mm, "dz" : 0 * mm, "makeCopy" : true});
        }
        {
            var Q0;
            Q0=makeQuery(id+"F37.opExtrude","SWEPT_BODY",BODY,{"disambiguationData":[OSD([sQuery(id+"F36.wireOp",EDGE,"E49")])]});
            var Q1;
            Q1=makeQuery(id+"F42.opPattern","COPY",BODY,{"derivedFrom":makeQuery(id+"F37.opExtrude","SWEPT_BODY",BODY,{"disambiguationData":[OSD([sQuery(id+"F36.wireOp",EDGE,"E49")])]}),"instanceName":"1"});
            transform(context, id + "F43", {"entities" : qUnion([Q0, Q1]), "transformType" : TransformType.TRANSLATION_3D, "dx" : 0 * mm, "dy" : 2320 * mm, "dz" : 0 * mm, "makeCopy" : true});
        }
        {
            var Q0;
            Q0=makeQuery(id+"F37.opExtrude","SWEPT_BODY",BODY,{"disambiguationData":[OSD([sQuery(id+"F36.wireOp",EDGE,"E49")])]});
            var Q1;
            Q1=makeQuery(id+"F43.opPattern","COPY",BODY,{"derivedFrom":makeQuery(id+"F42.opPattern","COPY",BODY,{"derivedFrom":makeQuery(id+"F37.opExtrude","SWEPT_BODY",BODY,{"disambiguationData":[OSD([sQuery(id+"F36.wireOp",EDGE,"E49")])]}),"instanceName":"1"}),"instanceName":"1"});
            var Q2;
            Q2=makeQuery(id+"F42.opPattern","COPY",BODY,{"derivedFrom":makeQuery(id+"F37.opExtrude","SWEPT_BODY",BODY,{"disambiguationData":[OSD([sQuery(id+"F36.wireOp",EDGE,"E49")])]}),"instanceName":"1"});
            var Q3;
            Q3=makeQuery(id+"F43.opPattern","COPY",BODY,{"derivedFrom":makeQuery(id+"F37.opExtrude","SWEPT_BODY",BODY,{"disambiguationData":[OSD([sQuery(id+"F36.wireOp",EDGE,"E49")])]}),"instanceName":"1"});
            transform(context, id + "F44", {"entities" : qUnion([Q0, Q1, Q2, Q3]), "transformType" : TransformType.TRANSLATION_3D, "dx" : 0 * mm, "dy" : 4800 * mm, "dz" : 0 * mm, "makeCopy" : true});
        }
        {
            var Q0;
            Q0=makeQuery(id+"F37.opExtrude","SWEPT_BODY",BODY,{"disambiguationData":[OSD([sQuery(id+"F36.wireOp",EDGE,"E49")])]});
            var Q1;
            Q1=makeQuery(id+"F43.opPattern","COPY",BODY,{"derivedFrom":makeQuery(id+"F42.opPattern","COPY",BODY,{"derivedFrom":makeQuery(id+"F37.opExtrude","SWEPT_BODY",BODY,{"disambiguationData":[OSD([sQuery(id+"F36.wireOp",EDGE,"E49")])]}),"instanceName":"1"}),"instanceName":"1"});
            var Q2;
            Q2=makeQuery(id+"F44.opPattern","COPY",BODY,{"derivedFrom":makeQuery(id+"F43.opPattern","COPY",BODY,{"derivedFrom":makeQuery(id+"F42.opPattern","COPY",BODY,{"derivedFrom":makeQuery(id+"F37.opExtrude","SWEPT_BODY",BODY,{"disambiguationData":[OSD([sQuery(id+"F36.wireOp",EDGE,"E49")])]}),"instanceName":"1"}),"instanceName":"1"}),"instanceName":"1"});
            var Q3;
            Q3=makeQuery(id+"F44.opPattern","COPY",BODY,{"derivedFrom":makeQuery(id+"F43.opPattern","COPY",BODY,{"derivedFrom":makeQuery(id+"F37.opExtrude","SWEPT_BODY",BODY,{"disambiguationData":[OSD([sQuery(id+"F36.wireOp",EDGE,"E49")])]}),"instanceName":"1"}),"instanceName":"1"});
            var Q4;
            Q4=makeQuery(id+"F42.opPattern","COPY",BODY,{"derivedFrom":makeQuery(id+"F37.opExtrude","SWEPT_BODY",BODY,{"disambiguationData":[OSD([sQuery(id+"F36.wireOp",EDGE,"E49")])]}),"instanceName":"1"});
            var Q5;
            Q5=makeQuery(id+"F43.opPattern","COPY",BODY,{"derivedFrom":makeQuery(id+"F37.opExtrude","SWEPT_BODY",BODY,{"disambiguationData":[OSD([sQuery(id+"F36.wireOp",EDGE,"E49")])]}),"instanceName":"1"});
            var Q6;
            Q6=makeQuery(id+"F44.opPattern","COPY",BODY,{"derivedFrom":makeQuery(id+"F42.opPattern","COPY",BODY,{"derivedFrom":makeQuery(id+"F37.opExtrude","SWEPT_BODY",BODY,{"disambiguationData":[OSD([sQuery(id+"F36.wireOp",EDGE,"E49")])]}),"instanceName":"1"}),"instanceName":"1"});
            var Q7;
            Q7=makeQuery(id+"F44.opPattern","COPY",BODY,{"derivedFrom":makeQuery(id+"F37.opExtrude","SWEPT_BODY",BODY,{"disambiguationData":[OSD([sQuery(id+"F36.wireOp",EDGE,"E49")])]}),"instanceName":"1"});
            transform(context, id + "F45", {"entities" : qUnion([Q0, Q1, Q2, Q3, Q4, Q5, Q6, Q7]), "transformType" : TransformType.TRANSLATION_3D, "dx" : 22100 * mm, "dy" : 0 * mm, "dz" : 0 * mm, "makeCopy" : true});
        }
        {
            var Q0;
            Q0=makeQuery(id+"F32.imprint","IMPRINT",FACE,{"disambiguationData":[TD([[makeQuery(id+"F32.imprint","IMPRINT",EDGE,{"derivedFrom":makeQuery(id+"F27.imprint","IMPRINT",EDGE,{"derivedFrom":makeQuery(id+"F1.opExtrude","CAP_EDGE",EDGE,{"disambiguationData":[OSD([sQuery(id+"F0.wireOp",EDGE,"E0")])],"isStart":false})})}),1.0]])]});
            var sketch = newSketch(context, id + "F46", { "sketchPlane" : qUnion([Q0])});
            skLineSegment(sketch, "E50.bottom", {"start": v(11274, 14455) * mm, "end": v(10574, 14455) * mm});
            skLineSegment(sketch, "E50.top", {"start": v(11274, 15905) * mm, "end": v(10574, 15905) * mm});
            skLineSegment(sketch, "E50.left", {"start": v(11274, 14455) * mm, "end": v(11274, 15905) * mm});
            skLineSegment(sketch, "E50.right", {"start": v(10574, 14455) * mm, "end": v(10574, 15905) * mm});
            skPoint(sketch, "E50.middle", {"position": v(10924, 15180) * mm});
            skLineSegment(sketch, "E51.bottom", {"start": v(21520, 22140) * mm, "end": v(20020, 22140) * mm});
            skLineSegment(sketch, "E51.top", {"start": v(21520, 25140) * mm, "end": v(20020, 25140) * mm});
            skLineSegment(sketch, "E51.left", {"start": v(21520, 22140) * mm, "end": v(21520, 25140) * mm});
            skLineSegment(sketch, "E51.right", {"start": v(20020, 22140) * mm, "end": v(20020, 25140) * mm});
            skPoint(sketch, "E51.middle", {"position": v(20770, 23640) * mm});
            skSolve(sketch);
        }
        {
            var Q0;
            Q0=makeQuery(id+"F46.imprint","IMPRINT",FACE,{"disambiguationData":[TD([[makeQuery(id+"F46.imprint","IMPRINT",EDGE,{"derivedFrom":sQuery(id+"F46.wireOp",EDGE,"E51.bottom")}),-1.0]])]});
            var Q1;
            Q1=makeQuery(id+"F46.imprint","IMPRINT",FACE,{"disambiguationData":[TD([[makeQuery(id+"F46.imprint","IMPRINT",EDGE,{"derivedFrom":sQuery(id+"F46.wireOp",EDGE,"E50.bottom")}),-1.0]])]});
            extrude(context, id + "F47", {"entities" : qUnion([Q0, Q1]), "depth" : 1200 * mm, "offsetDistance" : 25 * mm});
        }
    });
